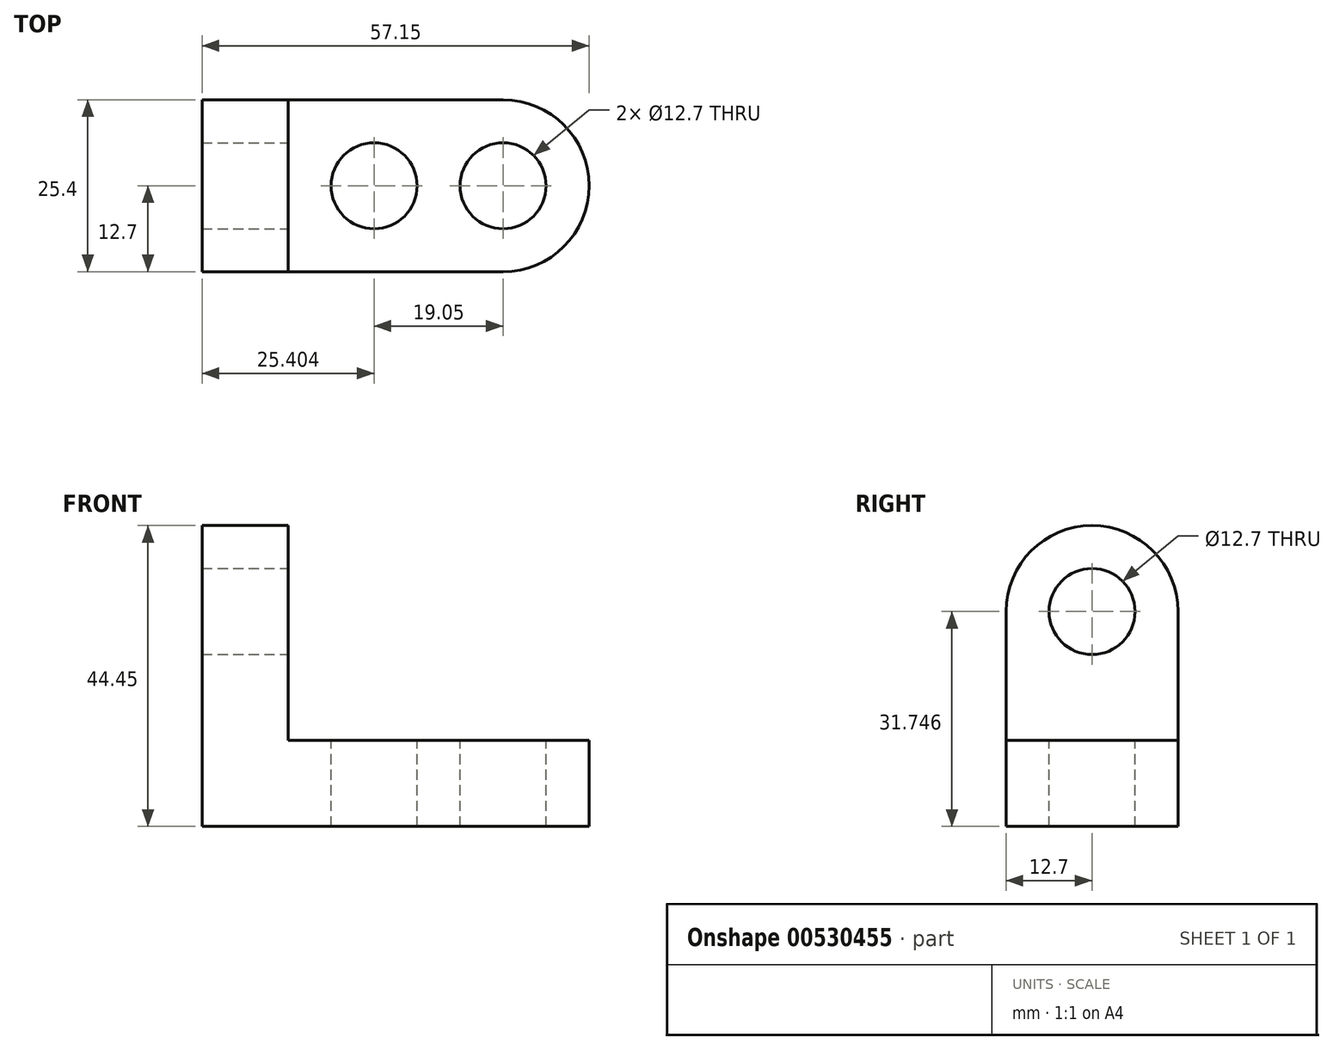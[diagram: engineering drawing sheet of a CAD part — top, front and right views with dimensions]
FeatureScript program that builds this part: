
annotation { "Feature Type Name" : "Feature", "Feature Type Description" : "" }
export const myFeature = defineFeature(function(context is Context, id is Id, definition is map)
    precondition{}
    {
        {
            var Q0;
            Q0=qCreatedBy(makeId("Front.planeOp"),FACE);
            var sketch = newSketch(context, id + "F0", { "sketchPlane" : qUnion([Q0])});
            skLineSegment(sketch, "E0", {"start": v(-14.94, 8.37) * mm, "end": v(-72.09, 8.37) * mm});
            skLineSegment(sketch, "E1", {"start": v(-72.09, 8.37) * mm, "end": v(-72.09, 52.82) * mm});
            skLineSegment(sketch, "E2", {"start": v(-72.09, 52.82) * mm, "end": v(-59.39, 52.82) * mm});
            skLineSegment(sketch, "E3", {"start": v(-59.39, 52.82) * mm, "end": v(-59.39, 21.07) * mm});
            skLineSegment(sketch, "E4", {"start": v(-59.39, 21.07) * mm, "end": v(-14.94, 21.07) * mm});
            skLineSegment(sketch, "E5", {"start": v(-14.94, 21.07) * mm, "end": v(-14.94, 8.37) * mm});
            skSolve(sketch);
        }
        {
            var Q0;
            Q0=makeQuery(id+"F0.imprint","IMPRINT",FACE,{"disambiguationData":[TD([[makeQuery(id+"F0.imprint","IMPRINT",EDGE,{"derivedFrom":sQuery(id+"F0.wireOp",EDGE,"E0")}),-1.0]])]});
            extrude(context, id + "F1", {"entities" : qUnion([Q0]), "depth" : 25.4 * mm, "offsetDistance" : 25.4 * mm});
        }
        {
            var Q0;
            Q0=makeQuery(id+"F1.opExtrude","SWEPT_FACE",FACE,{"disambiguationData":[OSD([sQuery(id+"F0.wireOp",EDGE,"E4")])]});
            var sketch = newSketch(context, id + "F2", { "sketchPlane" : qUnion([Q0])});
            skCircle(sketch, "E6", {"center": v(-27.64, -12.7) * mm, "radius": 6.35 * mm});
            skCircle(sketch, "E7", {"center": v(-46.69, -12.7) * mm, "radius": 6.35 * mm});
            skSolve(sketch);
        }
        {
            var Q0;
            Q0=makeQuery(id+"F2.imprint","IMPRINT",FACE,{"disambiguationData":[TD([[makeQuery(id+"F2.imprint","IMPRINT",EDGE,{"derivedFrom":sQuery(id+"F2.wireOp",EDGE,"E7")}),1.0]])]});
            var Q1;
            Q1=makeQuery(id+"F2.imprint","IMPRINT",FACE,{"disambiguationData":[TD([[makeQuery(id+"F2.imprint","IMPRINT",EDGE,{"derivedFrom":sQuery(id+"F2.wireOp",EDGE,"E6")}),1.0]])]});
            extrude(context, id + "F3", {"entities" : qUnion([Q0, Q1]), "operationType" : NewBodyOperationType.REMOVE, "endBound" : BoundingType.THROUGH_ALL, "oppositeDirection" : true, "depth" : 25.4 * mm, "offsetDistance" : 25.4 * mm});
        }
        {
            var Q0;
            Q0=makeQuery(id+"F1.opExtrude","SWEPT_FACE",FACE,{"disambiguationData":[OSD([sQuery(id+"F0.wireOp",EDGE,"E4")])]});
            var sketch = newSketch(context, id + "F4", { "sketchPlane" : qUnion([Q0])});
            skArc(sketch, "E8", {"start": v(-27.64, -25.4) * mm, "mid": v(-14.94, -12.7) * mm, "end": v(-27.64, 0) * mm});
            skSolve(sketch);
        }
        {
            var Q0;
            {var subQ0=sQuery(id+"F4.wireOp",EDGE,"E8");var subQ1=sQuery(id+"F0.wireOp",EDGE,"E4");var subQ2=makeQuery(id+"F1.opExtrude","CAP_EDGE",EDGE,{"disambiguationData":[OSD([subQ1])],"isStart":true});var subQ3=makeQuery(id+"F4.imprint","INTERSECT",VERTEX,{"derivedFrom":[subQ2,subQ0]});Q0=makeQuery(id+"F4.imprint","IMPRINT",FACE,{"disambiguationData":[TD([[makeQuery(id+"F4.imprint","IMPRINT",EDGE,{"disambiguationData":[TD([[subQ3,1.0]])],"derivedFrom":subQ0}),-1.0]])]});}
            var Q1;
            {var subQ0=sQuery(id+"F4.wireOp",EDGE,"E8");var subQ1=sQuery(id+"F0.wireOp",EDGE,"E4");var subQ2=makeQuery(id+"F1.opExtrude","CAP_EDGE",EDGE,{"disambiguationData":[OSD([subQ1])],"isStart":false});var subQ3=makeQuery(id+"F4.imprint","INTERSECT",VERTEX,{"derivedFrom":[subQ2,subQ0]});Q1=makeQuery(id+"F4.imprint","IMPRINT",FACE,{"disambiguationData":[TD([[makeQuery(id+"F4.imprint","IMPRINT",EDGE,{"disambiguationData":[TD([[subQ3,-1.0]])],"derivedFrom":subQ0}),-1.0]])]});}
            extrude(context, id + "F5", {"entities" : qUnion([Q0, Q1]), "operationType" : NewBodyOperationType.REMOVE, "endBound" : BoundingType.THROUGH_ALL, "oppositeDirection" : true, "depth" : 25.4 * mm, "offsetDistance" : 25.4 * mm});
        }
        {
            var Q0;
            Q0=makeQuery(id+"F1.opExtrude","SWEPT_FACE",FACE,{"disambiguationData":[OSD([sQuery(id+"F0.wireOp",EDGE,"E3")])]});
            var sketch = newSketch(context, id + "F6", { "sketchPlane" : qUnion([Q0])});
            skArc(sketch, "E9", {"start": v(0, 40.12) * mm, "mid": v(-12.7, 52.82) * mm, "end": v(-25.4, 40.12) * mm});
            skSolve(sketch);
        }
        {
            var Q0;
            {var subQ0=sQuery(id+"F6.wireOp",EDGE,"E9");var subQ1=sQuery(id+"F0.wireOp",EDGE,"E3");var subQ2=makeQuery(id+"F1.opExtrude","CAP_EDGE",EDGE,{"disambiguationData":[OSD([subQ1])],"isStart":false});var subQ3=makeQuery(id+"F6.imprint","INTERSECT",VERTEX,{"derivedFrom":[subQ2,subQ0]});Q0=makeQuery(id+"F6.imprint","IMPRINT",FACE,{"disambiguationData":[TD([[makeQuery(id+"F6.imprint","IMPRINT",EDGE,{"disambiguationData":[TD([[subQ3,1.0]])],"derivedFrom":subQ0}),-1.0]])]});}
            var Q1;
            {var subQ0=sQuery(id+"F6.wireOp",EDGE,"E9");var subQ1=sQuery(id+"F0.wireOp",EDGE,"E3");var subQ2=makeQuery(id+"F1.opExtrude","CAP_EDGE",EDGE,{"disambiguationData":[OSD([subQ1])],"isStart":true});var subQ3=makeQuery(id+"F6.imprint","INTERSECT",VERTEX,{"derivedFrom":[subQ2,subQ0]});Q1=makeQuery(id+"F6.imprint","IMPRINT",FACE,{"disambiguationData":[TD([[makeQuery(id+"F6.imprint","IMPRINT",EDGE,{"disambiguationData":[TD([[subQ3,-1.0]])],"derivedFrom":subQ0}),-1.0]])]});}
            extrude(context, id + "F7", {"entities" : qUnion([Q0, Q1]), "operationType" : NewBodyOperationType.REMOVE, "endBound" : BoundingType.THROUGH_ALL, "oppositeDirection" : true, "depth" : 25.4 * mm, "offsetDistance" : 25.4 * mm});
        }
        {
            var Q0;
            Q0=makeQuery(id+"F1.opExtrude","SWEPT_FACE",FACE,{"disambiguationData":[OSD([sQuery(id+"F0.wireOp",EDGE,"E3")])]});
            var sketch = newSketch(context, id + "F8", { "sketchPlane" : qUnion([Q0])});
            skCircle(sketch, "E10", {"center": v(-12.7, 40.12) * mm, "radius": 6.35 * mm});
            skLineSegment(sketch, "E11", {"start": v(-12.7, 40.12) * mm, "end": v(-19.05, 40.12) * mm});
            skLineSegment(sketch, "E12", {"start": v(-19.05, 40.12) * mm, "end": v(-19.05, 51.11) * mm});
            skLineSegment(sketch, "E13", {"start": v(-19.05, 51.11) * mm, "end": v(-19.05, 40.12) * mm});
            skLineSegment(sketch, "E14", {"start": v(-12.7, 40.12) * mm, "end": v(-6.35, 40.12) * mm});
            skLineSegment(sketch, "E15", {"start": v(-6.35, 40.12) * mm, "end": v(-6.35, 51.11) * mm});
            skSolve(sketch);
        }
        {
            var Q0;
            {var subQ0=sQuery(id+"F8.wireOp",EDGE,"E11");Q0=makeQuery(id+"F8.imprint","IMPRINT",FACE,{"disambiguationData":[TD([[makeQuery(id+"F8.imprint","IMPRINT",EDGE,{"derivedFrom":subQ0}),1.0]])]});}
            var Q1;
            {var subQ0=sQuery(id+"F8.wireOp",EDGE,"E13");Q1=makeQuery(id+"F8.imprint","IMPRINT",FACE,{"disambiguationData":[TD([[makeQuery(id+"F8.imprint","IMPRINT",EDGE,{"derivedFrom":subQ0}),1.0]])]});}
            var Q2;
            {var subQ0=sQuery(id+"F8.wireOp",EDGE,"E11");Q2=makeQuery(id+"F8.imprint","IMPRINT",FACE,{"disambiguationData":[TD([[makeQuery(id+"F8.imprint","IMPRINT",EDGE,{"derivedFrom":subQ0}),-1.0]])]});}
            extrude(context, id + "F9", {"entities" : qUnion([Q0, Q1, Q2]), "operationType" : NewBodyOperationType.REMOVE, "endBound" : BoundingType.THROUGH_ALL, "oppositeDirection" : true, "depth" : 25.4 * mm, "offsetDistance" : 25.4 * mm});
        }
    });
